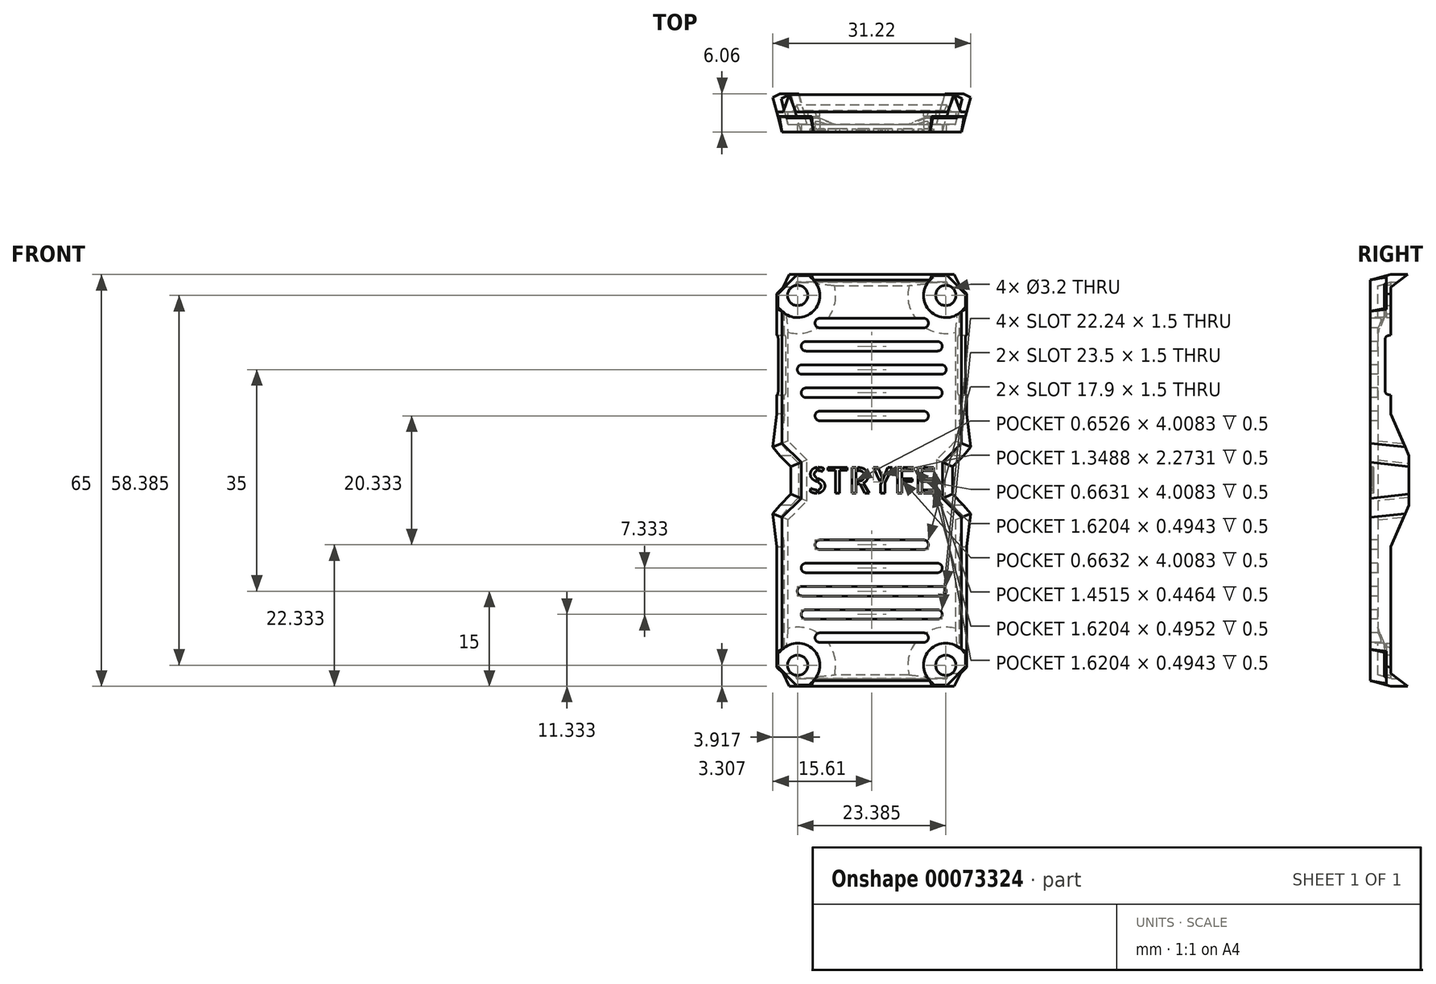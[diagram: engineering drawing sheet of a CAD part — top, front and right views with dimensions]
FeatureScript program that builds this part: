
annotation { "Feature Type Name" : "Feature", "Feature Type Description" : "" }
export const myFeature = defineFeature(function(context is Context, id is Id, definition is map)
    precondition{}
    {
        {
            var Q0;
            Q0=qCreatedBy(makeId("Front.planeOp"),FACE);
            var sketch = newSketch(context, id + "F0", { "sketchPlane" : qUnion([Q0])});
            skLineSegment(sketch, "E0.bottom", {"start": v(15, -32.5) * mm, "end": v(-15, -32.5) * mm});
            skLineSegment(sketch, "E0.top", {"start": v(15, 32.5) * mm, "end": v(-15, 32.5) * mm});
            skLineSegment(sketch, "E0.left", {"start": v(15, -32.5) * mm, "end": v(15, 32.5) * mm});
            skLineSegment(sketch, "E0.right", {"start": v(-15, -32.5) * mm, "end": v(-15, 32.5) * mm});
            skPoint(sketch, "E0.middle", {"position": v(0, 0) * mm});
            skSolve(sketch);
        }
        {
            var Q0;
            Q0=qCreatedBy(makeId("Front.planeOp"),FACE);
            var sketch = newSketch(context, id + "F1", { "sketchPlane" : qUnion([Q0])});
            skLineSegment(sketch, "E1", {"start": v(0, 32.5) * mm, "end": v(-12, 32.5) * mm});
            skLineSegment(sketch, "E2", {"start": v(-12, 32.5) * mm, "end": v(-15, 29.5) * mm});
            skLineSegment(sketch, "E3", {"start": v(-15, 29.5) * mm, "end": v(-15, 5.5) * mm});
            skLineSegment(sketch, "E4", {"start": v(-15, 5.5) * mm, "end": v(-12, 2.5) * mm});
            skLineSegment(sketch, "E5", {"start": v(-12, 2.5) * mm, "end": v(-12, 0) * mm});
            skLineSegment(sketch, "E6", {"start": v(-12, 2.5) * mm, "end": v(-15, 2.5) * mm, "construction": true});
            skLineSegment(sketch, "E7", {"start": v(-15, 2.5) * mm, "end": v(-15, 5.5) * mm, "construction": true});
            skLineSegment(sketch, "E8", {"start": v(-15, 29.5) * mm, "end": v(-15, 32.5) * mm, "construction": true});
            skLineSegment(sketch, "E9", {"start": v(-15, 32.5) * mm, "end": v(-12, 32.5) * mm, "construction": true});
            skLineSegment(sketch, "E10.MirrorCS", {"start": v(0, 32.5) * mm, "end": v(12, 32.5) * mm});
            skLineSegment(sketch, "E11.MirrorCS", {"start": v(12, 2.5) * mm, "end": v(12, 0) * mm});
            skLineSegment(sketch, "E12.MirrorCS", {"start": v(15, 5.5) * mm, "end": v(12, 2.5) * mm});
            skLineSegment(sketch, "E13.MirrorCS", {"start": v(12, 32.5) * mm, "end": v(15, 29.5) * mm});
            skLineSegment(sketch, "E14.MirrorCS", {"start": v(15, 29.5) * mm, "end": v(15, 5.5) * mm});
            skLineSegment(sketch, "E15.MirrorCS", {"start": v(12, -2.5) * mm, "end": v(12, 0) * mm});
            skLineSegment(sketch, "E16.MirrorCS", {"start": v(15, -5.5) * mm, "end": v(12, -2.5) * mm});
            skLineSegment(sketch, "E17.MirrorCS", {"start": v(15, -29.5) * mm, "end": v(15, -5.5) * mm});
            skLineSegment(sketch, "E18.MirrorCS", {"start": v(12, -32.5) * mm, "end": v(15, -29.5) * mm});
            skLineSegment(sketch, "E19.MirrorCS", {"start": v(0, -32.5) * mm, "end": v(12, -32.5) * mm});
            skLineSegment(sketch, "E20.MirrorCS", {"start": v(0, -32.5) * mm, "end": v(-12, -32.5) * mm});
            skLineSegment(sketch, "E21.MirrorCS", {"start": v(-12, -32.5) * mm, "end": v(-15, -29.5) * mm});
            skLineSegment(sketch, "E22.MirrorCS", {"start": v(-15, -29.5) * mm, "end": v(-15, -5.5) * mm});
            skLineSegment(sketch, "E23.MirrorCS", {"start": v(-12, -2.5) * mm, "end": v(-12, 0) * mm});
            skLineSegment(sketch, "E24.MirrorCS", {"start": v(-15, -5.5) * mm, "end": v(-12, -2.5) * mm});
            skLineSegment(sketch, "E25", {"start": v(-12, 32.5) * mm, "end": v(12, 32.5) * mm, "construction": true});
            skSolve(sketch);
        }
        {
            assignVariable(context, id + "F2", {"name" : "Draft", "anyValue" : 15});
        }
        {
            var Q0;
            Q0 = qSketchRegion(id + "F1", true);
            extrude(context, id + "F3", {"entities" : qUnion([Q0]), "depth" : 3.2 * mm, "hasDraft" : true, "draftAngle" : (getVariable(context, 'Draft')) * degree, "draftPullDirection" : true});
        }
        {
            var Q0;
            Q0=qCreatedBy(makeId("Front.planeOp"),FACE);
            var sketch = newSketch(context, id + "F4", { "sketchPlane" : qUnion([Q0])});
            skLineSegment(sketch, "E26.0.1", {"start": v(-15, -10.5) * mm, "end": v(-15, -5.5) * mm});
            skLineSegment(sketch, "E26.0.2", {"start": v(-15, -5.5) * mm, "end": v(-12, -2.5) * mm});
            skLineSegment(sketch, "E26.0.3", {"start": v(-12, 2.5) * mm, "end": v(-12, -2.5) * mm});
            skLineSegment(sketch, "E26.0.4", {"start": v(-15, 5.5) * mm, "end": v(-12, 2.5) * mm});
            skLineSegment(sketch, "E26.0.5", {"start": v(-15, 10.5) * mm, "end": v(-15, 5.5) * mm});
            skLineSegment(sketch, "E26.0.9", {"start": v(15, 10.5) * mm, "end": v(15, 5.5) * mm});
            skLineSegment(sketch, "E26.0.10", {"start": v(15, 5.5) * mm, "end": v(12, 2.5) * mm});
            skLineSegment(sketch, "E26.0.11", {"start": v(12, -2.5) * mm, "end": v(12, 2.5) * mm});
            skLineSegment(sketch, "E26.0.12", {"start": v(15, -5.5) * mm, "end": v(12, -2.5) * mm});
            skLineSegment(sketch, "E26.0.13", {"start": v(15, -10.5) * mm, "end": v(15, -5.5) * mm});
            skLineSegment(sketch, "E27", {"start": v(15, 10.5) * mm, "end": v(-15, 10.5) * mm});
            skLineSegment(sketch, "E28", {"start": v(-15, -10.5) * mm, "end": v(15, -10.5) * mm});
            skLineSegment(sketch, "E29", {"start": v(0, 0) * mm, "end": v(0, 10.5) * mm, "construction": true});
            skLineSegment(sketch, "E30", {"start": v(0, 0) * mm, "end": v(0, -10.5) * mm, "construction": true});
            skSolve(sketch);
        }
        {
            var Q0;
            Q0 = qSketchRegion(id + "F4", true);
            extrude(context, id + "F5", {"entities" : qUnion([Q0]), "operationType" : NewBodyOperationType.ADD, "oppositeDirection" : true, "depth" : 2.86 * mm, "hasDraft" : true, "draftAngle" : (getVariable(context, 'Draft')) * degree});
        }
        {
            var Q0;
            Q0=qCreatedBy(makeId("Right.planeOp"),FACE);
            var sketch = newSketch(context, id + "F6", { "sketchPlane" : qUnion([Q0])});
            skLineSegment(sketch, "E31", {"start": v(0, 10.5) * mm, "end": v(2.86, 3.9) * mm});
            skLineSegment(sketch, "E32", {"start": v(2.86, 3.9) * mm, "end": v(2.86, 0) * mm});
            skLineSegment(sketch, "E33", {"start": v(2.86, 0) * mm, "end": v(0, 0) * mm, "construction": true});
            skLineSegment(sketch, "E34.MirrorCS", {"start": v(0, -10.5) * mm, "end": v(2.86, -3.9) * mm});
            skLineSegment(sketch, "E35.MirrorCS", {"start": v(2.86, -3.9) * mm, "end": v(2.86, 0) * mm});
            skLineSegment(sketch, "E36.0", {"start": v(2.86, 11.27) * mm, "end": v(0, 10.5) * mm});
            skLineSegment(sketch, "E36.1", {"start": v(2.86, -11.27) * mm, "end": v(0, -10.5) * mm});
            skLineSegment(sketch, "E37", {"start": v(2.86, -11.27) * mm, "end": v(2.86, -3.9) * mm});
            skLineSegment(sketch, "E38", {"start": v(2.86, 3.9) * mm, "end": v(2.86, 11.27) * mm});
            skSolve(sketch);
        }
        {
            var Q0;
            Q0 = qSketchRegion(id + "F6", true);
            extrude(context, id + "F7", {"entities" : qUnion([Q0]), "operationType" : NewBodyOperationType.REMOVE, "endBound" : BoundingType.THROUGH_ALL, "depth" : 25 * mm, "hasSecondDirection" : true, "secondDirectionBound" : SecondDirectionBoundingType.THROUGH_ALL, "secondDirectionOppositeDirection" : true, "secondDirectionDepth" : 25 * mm});
        }
        {
            var Q0;
            Q0=qCreatedBy(makeId("Right.planeOp"),FACE);
            var sketch = newSketch(context, id + "F8", { "sketchPlane" : qUnion([Q0])});
            skLineSegment(sketch, "E39", {"start": v(0, 32.5) * mm, "end": v(0, 30.5) * mm});
            skLineSegment(sketch, "E40", {"start": v(0, 30.5) * mm, "end": v(2.7, 32.5) * mm});
            skLineSegment(sketch, "E41", {"start": v(2.7, 32.5) * mm, "end": v(0, 32.5) * mm});
            skLineSegment(sketch, "E42.MirrorCS", {"start": v(0, -32.5) * mm, "end": v(0, -30.5) * mm, "construction": true});
            skLineSegment(sketch, "E43.MirrorCS", {"start": v(0, -30.5) * mm, "end": v(2.7, -32.5) * mm, "construction": true});
            skLineSegment(sketch, "E44.MirrorCS", {"start": v(2.7, -32.5) * mm, "end": v(0, -32.5) * mm, "construction": true});
            skSolve(sketch);
        }
        {
            var Q0;
            Q0 = qSketchRegion(id + "F8", true);
            var Q1;
            Q1=makeQuery(id+"F3.opExtrude","SWEPT_FACE",FACE,{"disambiguationData":[OSD([sQuery(id+"F1.wireOp",EDGE,"E13.MirrorCS")])]});
            var Q2;
            Q2=makeQuery(id+"F3.opExtrude","SWEPT_BODY",BODY,{"disambiguationData":[OSD([sQuery(id+"F1.wireOp",EDGE,"E1"),sQuery(id+"F1.wireOp",EDGE,"E2"),sQuery(id+"F1.wireOp",EDGE,"E3"),sQuery(id+"F1.wireOp",EDGE,"E4"),sQuery(id+"F1.wireOp",EDGE,"E5"),sQuery(id+"F1.wireOp",EDGE,"E10.MirrorCS"),sQuery(id+"F1.wireOp",EDGE,"E11.MirrorCS"),sQuery(id+"F1.wireOp",EDGE,"E12.MirrorCS"),sQuery(id+"F1.wireOp",EDGE,"E13.MirrorCS"),sQuery(id+"F1.wireOp",EDGE,"E14.MirrorCS"),sQuery(id+"F1.wireOp",EDGE,"E15.MirrorCS"),sQuery(id+"F1.wireOp",EDGE,"E16.MirrorCS"),sQuery(id+"F1.wireOp",EDGE,"E17.MirrorCS"),sQuery(id+"F1.wireOp",EDGE,"E18.MirrorCS"),sQuery(id+"F1.wireOp",EDGE,"E19.MirrorCS"),sQuery(id+"F1.wireOp",EDGE,"E20.MirrorCS"),sQuery(id+"F1.wireOp",EDGE,"E21.MirrorCS"),sQuery(id+"F1.wireOp",EDGE,"E22.MirrorCS"),sQuery(id+"F1.wireOp",EDGE,"E23.MirrorCS"),sQuery(id+"F1.wireOp",EDGE,"E24.MirrorCS")])]});
            var Q3;
            Q3=makeQuery(id+"F3.opExtrude","SWEPT_FACE",FACE,{"disambiguationData":[OSD([sQuery(id+"F1.wireOp",EDGE,"E2")])]});
            extrude(context, id + "F9", {"entities" : qUnion([Q0]), "operationType" : NewBodyOperationType.ADD, "endBound" : BoundingType.UP_TO_SURFACE, "endBoundEntityFace" : qUnion([Q1]), "endBoundEntityBody" : qUnion([Q2]), "depth" : 25 * mm, "hasSecondDirection" : true, "secondDirectionBound" : SecondDirectionBoundingType.UP_TO_SURFACE, "secondDirectionOppositeDirection" : true, "secondDirectionBoundEntityFace" : qUnion([Q3]), "secondDirectionDepth" : 25 * mm});
        }
        {
            var Q0;
            Q0=qCreatedBy(makeId("Right.planeOp"),FACE);
            var sketch = newSketch(context, id + "F10", { "sketchPlane" : qUnion([Q0])});
            skLineSegment(sketch, "E45.0", {"start": v(0, -30.5) * mm, "end": v(2.7, -32.5) * mm});
            skLineSegment(sketch, "E45.1", {"start": v(0, -32.5) * mm, "end": v(0, -30.5) * mm});
            skLineSegment(sketch, "E45.2", {"start": v(2.7, -32.5) * mm, "end": v(0, -32.5) * mm});
            skSolve(sketch);
        }
        {
            var Q0;
            Q0 = qSketchRegion(id + "F10", true);
            var Q1;
            Q1=makeQuery(id+"F3.opExtrude","SWEPT_FACE",FACE,{"disambiguationData":[OSD([sQuery(id+"F1.wireOp",EDGE,"E21.MirrorCS")])]});
            var Q2;
            Q2=makeQuery(id+"F3.opExtrude","SWEPT_FACE",FACE,{"disambiguationData":[OSD([sQuery(id+"F1.wireOp",EDGE,"E18.MirrorCS")])]});
            extrude(context, id + "F11", {"entities" : qUnion([Q0]), "operationType" : NewBodyOperationType.ADD, "endBound" : BoundingType.UP_TO_SURFACE, "oppositeDirection" : true, "endBoundEntityFace" : qUnion([Q1]), "depth" : 25 * mm, "hasSecondDirection" : true, "secondDirectionBound" : SecondDirectionBoundingType.UP_TO_SURFACE, "secondDirectionOppositeDirection" : false, "secondDirectionBoundEntityFace" : qUnion([Q2]), "secondDirectionDepth" : 25 * mm});
        }
        {
            var Q0;
            {var subQ0=sQuery(id+"F1.wireOp",EDGE,"E3");var subQ1=sQuery(id+"F1.wireOp",EDGE,"E13.MirrorCS");var subQ2=sQuery(id+"F1.wireOp",EDGE,"E2");var subQ3=sQuery(id+"F1.wireOp",EDGE,"E10.MirrorCS");var subQ4=sQuery(id+"F1.wireOp",EDGE,"E1");var subQ5=sQuery(id+"F1.wireOp",EDGE,"E14.MirrorCS");Q0=makeQuery(id+"F5.boolean.opBoolean","SPLIT",FACE,{"disambiguationData":[TD([makeQuery(id+"F3.opExtrude","SWEPT_FACE",FACE,{"disambiguationData":[OSD([subQ2])]})])],"derivedFrom":makeQuery(id+"F3.opExtrude","CAP_FACE",FACE,{"disambiguationData":[OSD([subQ4,subQ2,subQ0,sQuery(id+"F1.wireOp",EDGE,"E4"),sQuery(id+"F1.wireOp",EDGE,"E5"),subQ3,sQuery(id+"F1.wireOp",EDGE,"E11.MirrorCS"),sQuery(id+"F1.wireOp",EDGE,"E12.MirrorCS"),subQ1,subQ5,sQuery(id+"F1.wireOp",EDGE,"E15.MirrorCS"),sQuery(id+"F1.wireOp",EDGE,"E16.MirrorCS"),sQuery(id+"F1.wireOp",EDGE,"E17.MirrorCS"),sQuery(id+"F1.wireOp",EDGE,"E18.MirrorCS"),sQuery(id+"F1.wireOp",EDGE,"E19.MirrorCS"),sQuery(id+"F1.wireOp",EDGE,"E20.MirrorCS"),sQuery(id+"F1.wireOp",EDGE,"E21.MirrorCS"),sQuery(id+"F1.wireOp",EDGE,"E22.MirrorCS"),sQuery(id+"F1.wireOp",EDGE,"E23.MirrorCS"),sQuery(id+"F1.wireOp",EDGE,"E24.MirrorCS")])],"isStart":true})});}
            var Q1;
            Q1=makeQuery(id+"F7.boolean.opBoolean","COPY",FACE,{"derivedFrom":makeQuery(id+"F7.opExtrude","SWEPT_FACE",FACE,{"disambiguationData":[OSD([sQuery(id+"F6.wireOp",EDGE,"E31")])]})});
            var Q2;
            Q2=makeQuery(id+"F5.opExtrude","CAP_FACE",FACE,{"disambiguationData":[OSD([sQuery(id+"F4.wireOp",EDGE,"E26.0.1"),sQuery(id+"F4.wireOp",EDGE,"E26.0.2"),sQuery(id+"F4.wireOp",EDGE,"E26.0.3"),sQuery(id+"F4.wireOp",EDGE,"E26.0.4"),sQuery(id+"F4.wireOp",EDGE,"E26.0.5"),sQuery(id+"F4.wireOp",EDGE,"E26.0.9"),sQuery(id+"F4.wireOp",EDGE,"E26.0.10"),sQuery(id+"F4.wireOp",EDGE,"E26.0.11"),sQuery(id+"F4.wireOp",EDGE,"E26.0.12"),sQuery(id+"F4.wireOp",EDGE,"E26.0.13"),sQuery(id+"F4.wireOp",EDGE,"E27"),sQuery(id+"F4.wireOp",EDGE,"E28")])],"isStart":false});
            var Q3;
            Q3=makeQuery(id+"F7.boolean.opBoolean","COPY",FACE,{"derivedFrom":makeQuery(id+"F7.opExtrude","SWEPT_FACE",FACE,{"disambiguationData":[OSD([sQuery(id+"F6.wireOp",EDGE,"E34.MirrorCS")])]})});
            var Q4;
            {var subQ0=sQuery(id+"F1.wireOp",EDGE,"E21.MirrorCS");var subQ1=sQuery(id+"F1.wireOp",EDGE,"E20.MirrorCS");var subQ2=sQuery(id+"F1.wireOp",EDGE,"E19.MirrorCS");var subQ3=sQuery(id+"F1.wireOp",EDGE,"E18.MirrorCS");var subQ4=sQuery(id+"F1.wireOp",EDGE,"E17.MirrorCS");var subQ5=sQuery(id+"F1.wireOp",EDGE,"E22.MirrorCS");Q4=makeQuery(id+"F5.boolean.opBoolean","SPLIT",FACE,{"disambiguationData":[TD([makeQuery(id+"F3.opExtrude","SWEPT_FACE",FACE,{"disambiguationData":[OSD([subQ4])]})])],"derivedFrom":makeQuery(id+"F3.opExtrude","CAP_FACE",FACE,{"disambiguationData":[OSD([sQuery(id+"F1.wireOp",EDGE,"E1"),sQuery(id+"F1.wireOp",EDGE,"E2"),sQuery(id+"F1.wireOp",EDGE,"E3"),sQuery(id+"F1.wireOp",EDGE,"E4"),sQuery(id+"F1.wireOp",EDGE,"E5"),sQuery(id+"F1.wireOp",EDGE,"E10.MirrorCS"),sQuery(id+"F1.wireOp",EDGE,"E11.MirrorCS"),sQuery(id+"F1.wireOp",EDGE,"E12.MirrorCS"),sQuery(id+"F1.wireOp",EDGE,"E13.MirrorCS"),sQuery(id+"F1.wireOp",EDGE,"E14.MirrorCS"),sQuery(id+"F1.wireOp",EDGE,"E15.MirrorCS"),sQuery(id+"F1.wireOp",EDGE,"E16.MirrorCS"),subQ4,subQ3,subQ2,subQ1,subQ0,subQ5,sQuery(id+"F1.wireOp",EDGE,"E23.MirrorCS"),sQuery(id+"F1.wireOp",EDGE,"E24.MirrorCS")])],"isStart":true})});}
            var Q5;
            Q5=makeQuery(id+"F9.opExtrude","SWEPT_FACE",FACE,{"disambiguationData":[OSD([sQuery(id+"F8.wireOp",EDGE,"E40")])]});
            var Q6;
            Q6=makeQuery(id+"F11.opExtrude","SWEPT_FACE",FACE,{"disambiguationData":[OSD([sQuery(id+"F10.wireOp",EDGE,"E45.0")])]});
            shell(context, id + "F12", {"entities" : qUnion([Q0, Q1, Q2, Q3, Q4, Q5, Q6]), "thickness" : 1.2 * mm});
        }
        {
            var Q0;
            Q0=qCreatedBy(makeId("Right.planeOp"),FACE);
            var sketch = newSketch(context, id + "F13", { "sketchPlane" : qUnion([Q0])});
            skLineSegment(sketch, "E46.bottom", {"start": v(0, 22.9) * mm, "end": v(-0.2, 22.9) * mm});
            skLineSegment(sketch, "E46.top", {"start": v(0, 13.5) * mm, "end": v(-0.2, 13.5) * mm});
            skLineSegment(sketch, "E46.left", {"start": v(0, 22.9) * mm, "end": v(0, 13.5) * mm});
            skLineSegment(sketch, "E46.right", {"start": v(-0.9, 22.2) * mm, "end": v(-0.9, 14.2) * mm});
            skPoint(sketch, "E47.visualSharp", {"position": v(-0.9, 22.9) * mm});
            skArc(sketch, "E47.filletArc", {"start": v(-0.2, 22.9) * mm, "mid": v(-0.7, 22.7) * mm, "end": v(-0.9, 22.2) * mm});
            skPoint(sketch, "E48.visualSharp", {"position": v(-0.9, 13.5) * mm});
            skArc(sketch, "E48.filletArc", {"start": v(-0.9, 14.2) * mm, "mid": v(-0.7, 13.7) * mm, "end": v(-0.2, 13.5) * mm});
            skSolve(sketch);
        }
        {
            var Q0;
            Q0 = qSketchRegion(id + "F13", true);
            extrude(context, id + "F14", {"entities" : qUnion([Q0]), "operationType" : NewBodyOperationType.REMOVE, "endBound" : BoundingType.THROUGH_ALL, "oppositeDirection" : true, "depth" : 25 * mm, "hasSecondDirection" : true, "secondDirectionBound" : SecondDirectionBoundingType.THROUGH_ALL, "secondDirectionOppositeDirection" : false, "secondDirectionDepth" : 25 * mm});
        }
        {
            var Q0;
            Q0=makeQuery(id+"F3.opExtrude","CAP_FACE",FACE,{"disambiguationData":[OSD([sQuery(id+"F1.wireOp",EDGE,"E1"),sQuery(id+"F1.wireOp",EDGE,"E2"),sQuery(id+"F1.wireOp",EDGE,"E3"),sQuery(id+"F1.wireOp",EDGE,"E4"),sQuery(id+"F1.wireOp",EDGE,"E5"),sQuery(id+"F1.wireOp",EDGE,"E10.MirrorCS"),sQuery(id+"F1.wireOp",EDGE,"E11.MirrorCS"),sQuery(id+"F1.wireOp",EDGE,"E12.MirrorCS"),sQuery(id+"F1.wireOp",EDGE,"E13.MirrorCS"),sQuery(id+"F1.wireOp",EDGE,"E14.MirrorCS"),sQuery(id+"F1.wireOp",EDGE,"E15.MirrorCS"),sQuery(id+"F1.wireOp",EDGE,"E16.MirrorCS"),sQuery(id+"F1.wireOp",EDGE,"E17.MirrorCS"),sQuery(id+"F1.wireOp",EDGE,"E18.MirrorCS"),sQuery(id+"F1.wireOp",EDGE,"E19.MirrorCS"),sQuery(id+"F1.wireOp",EDGE,"E20.MirrorCS"),sQuery(id+"F1.wireOp",EDGE,"E21.MirrorCS"),sQuery(id+"F1.wireOp",EDGE,"E22.MirrorCS"),sQuery(id+"F1.wireOp",EDGE,"E23.MirrorCS"),sQuery(id+"F1.wireOp",EDGE,"E24.MirrorCS")])],"isStart":false});
            var sketch = newSketch(context, id + "F15", { "sketchPlane" : qUnion([Q0])});
            skCircle(sketch, "E49", {"center": v(-11.7, 29.2) * mm, "radius": 3.5 * mm});
            skCircle(sketch, "E50", {"center": v(-11.7, 29.2) * mm, "radius": 1.6 * mm});
            skCircle(sketch, "E51", {"center": v(-11.7, 29.2) * mm, "radius": 4 * mm});
            skCircle(sketch, "E52.MirrorC", {"center": v(11.7, 29.2) * mm, "radius": 1.6 * mm});
            skCircle(sketch, "E53.MirrorC", {"center": v(11.7, 29.2) * mm, "radius": 3.5 * mm});
            skCircle(sketch, "E54.MirrorC", {"center": v(11.7, 29.2) * mm, "radius": 4 * mm});
            skCircle(sketch, "E55.MirrorC", {"center": v(11.7, -29.2) * mm, "radius": 1.6 * mm});
            skCircle(sketch, "E56.MirrorC", {"center": v(11.7, -29.2) * mm, "radius": 3.5 * mm});
            skCircle(sketch, "E57.MirrorC", {"center": v(11.7, -29.2) * mm, "radius": 4 * mm});
            skCircle(sketch, "E58.MirrorC", {"center": v(-11.7, -29.2) * mm, "radius": 1.6 * mm});
            skCircle(sketch, "E59.MirrorC", {"center": v(-11.7, -29.2) * mm, "radius": 3.5 * mm});
            skCircle(sketch, "E60.MirrorC", {"center": v(-11.7, -29.2) * mm, "radius": 4 * mm});
            skSolve(sketch);
        }
        {
            var Q0;
            Q0=makeQuery(id+"F15.imprint","IMPRINT",FACE,{"disambiguationData":[TD([[makeQuery(id+"F15.imprint","IMPRINT",EDGE,{"derivedFrom":sQuery(id+"F15.wireOp",EDGE,"E51")}),-1.0]])]});
            var sketch = newSketch(context, id + "F16", { "sketchPlane" : qUnion([Q0])});
            skCircle(sketch, "E61.0", {"center": v(-11.7, 29.2) * mm, "radius": 1.6 * mm});
            skCircle(sketch, "E61.1", {"center": v(11.7, 29.2) * mm, "radius": 1.6 * mm});
            skCircle(sketch, "E61.2", {"center": v(11.7, -29.2) * mm, "radius": 1.6 * mm});
            skCircle(sketch, "E61.3", {"center": v(-11.7, -29.2) * mm, "radius": 1.6 * mm});
            skSolve(sketch);
        }
        {
            var Q0;
            Q0=qCreatedBy(makeId("Front.planeOp"),FACE);
            var sketch = newSketch(context, id + "F17", { "sketchPlane" : qUnion([Q0])});
            skCircle(sketch, "E62.0", {"center": v(11.7, 29.2) * mm, "radius": 3.5 * mm});
            skCircle(sketch, "E62.1", {"center": v(-11.7, 29.2) * mm, "radius": 3.5 * mm});
            skCircle(sketch, "E62.2", {"center": v(-11.7, -29.2) * mm, "radius": 3.5 * mm});
            skCircle(sketch, "E62.3", {"center": v(11.7, -29.2) * mm, "radius": 3.5 * mm});
            skSolve(sketch);
        }
        {
            var Q0;
            Q0=makeQuery(id+"F15.imprint","IMPRINT",FACE,{"disambiguationData":[TD([[makeQuery(id+"F15.imprint","IMPRINT",EDGE,{"derivedFrom":sQuery(id+"F15.wireOp",EDGE,"E51")}),-1.0]])]});
            var sketch = newSketch(context, id + "F18", { "sketchPlane" : qUnion([Q0])});
            skCircle(sketch, "E63.0", {"center": v(-11.7, 29.2) * mm, "radius": 3.5 * mm});
            skCircle(sketch, "E63.1", {"center": v(11.7, 29.2) * mm, "radius": 3.5 * mm});
            skCircle(sketch, "E63.2", {"center": v(11.7, -29.2) * mm, "radius": 3.5 * mm});
            skCircle(sketch, "E63.3", {"center": v(-11.7, -29.2) * mm, "radius": 3.5 * mm});
            skSolve(sketch);
        }
        {
            var Q0;
            Q0 = qSketchRegion(id + "F17", true);
            var Q1;
            Q1=makeQuery(id+"F3.opExtrude","SWEPT_BODY",BODY,{"disambiguationData":[OSD([sQuery(id+"F1.wireOp",EDGE,"E1"),sQuery(id+"F1.wireOp",EDGE,"E2"),sQuery(id+"F1.wireOp",EDGE,"E3"),sQuery(id+"F1.wireOp",EDGE,"E4"),sQuery(id+"F1.wireOp",EDGE,"E5"),sQuery(id+"F1.wireOp",EDGE,"E10.MirrorCS"),sQuery(id+"F1.wireOp",EDGE,"E11.MirrorCS"),sQuery(id+"F1.wireOp",EDGE,"E12.MirrorCS"),sQuery(id+"F1.wireOp",EDGE,"E13.MirrorCS"),sQuery(id+"F1.wireOp",EDGE,"E14.MirrorCS"),sQuery(id+"F1.wireOp",EDGE,"E15.MirrorCS"),sQuery(id+"F1.wireOp",EDGE,"E16.MirrorCS"),sQuery(id+"F1.wireOp",EDGE,"E17.MirrorCS"),sQuery(id+"F1.wireOp",EDGE,"E18.MirrorCS"),sQuery(id+"F1.wireOp",EDGE,"E19.MirrorCS"),sQuery(id+"F1.wireOp",EDGE,"E20.MirrorCS"),sQuery(id+"F1.wireOp",EDGE,"E21.MirrorCS"),sQuery(id+"F1.wireOp",EDGE,"E22.MirrorCS"),sQuery(id+"F1.wireOp",EDGE,"E23.MirrorCS"),sQuery(id+"F1.wireOp",EDGE,"E24.MirrorCS")])]});
            extrude(context, id + "F19", {"entities" : qUnion([Q0]), "operationType" : NewBodyOperationType.ADD, "endBound" : BoundingType.UP_TO_BODY, "endBoundEntityBody" : qUnion([Q1]), "depth" : 25 * mm});
        }
        {
            var Q0;
            Q0=makeQuery(id+"F19.boolean.opBoolean","INTERSECT",EDGE,{"derivedFrom":[makeQuery(id+"F12.opShell","OFFSET_FACE",FACE,{"disambiguationData":[OSD([sQuery(id+"F1.wireOp",EDGE,"E1"),sQuery(id+"F1.wireOp",EDGE,"E2"),sQuery(id+"F1.wireOp",EDGE,"E3"),sQuery(id+"F1.wireOp",EDGE,"E4"),sQuery(id+"F1.wireOp",EDGE,"E5"),sQuery(id+"F1.wireOp",EDGE,"E10.MirrorCS"),sQuery(id+"F1.wireOp",EDGE,"E11.MirrorCS"),sQuery(id+"F1.wireOp",EDGE,"E12.MirrorCS"),sQuery(id+"F1.wireOp",EDGE,"E13.MirrorCS"),sQuery(id+"F1.wireOp",EDGE,"E14.MirrorCS"),sQuery(id+"F1.wireOp",EDGE,"E15.MirrorCS"),sQuery(id+"F1.wireOp",EDGE,"E16.MirrorCS"),sQuery(id+"F1.wireOp",EDGE,"E17.MirrorCS"),sQuery(id+"F1.wireOp",EDGE,"E18.MirrorCS"),sQuery(id+"F1.wireOp",EDGE,"E19.MirrorCS"),sQuery(id+"F1.wireOp",EDGE,"E20.MirrorCS"),sQuery(id+"F1.wireOp",EDGE,"E21.MirrorCS"),sQuery(id+"F1.wireOp",EDGE,"E22.MirrorCS"),sQuery(id+"F1.wireOp",EDGE,"E23.MirrorCS"),sQuery(id+"F1.wireOp",EDGE,"E24.MirrorCS")])]}),makeQuery(id+"F19.opExtrude","SWEPT_FACE",FACE,{"disambiguationData":[OSD([sQuery(id+"F17.wireOp",EDGE,"E62.0")])]})]});
            var Q1;
            Q1=makeQuery(id+"F19.boolean.opBoolean","INTERSECT",EDGE,{"derivedFrom":[makeQuery(id+"F12.opShell","OFFSET_FACE",FACE,{"disambiguationData":[OSD([sQuery(id+"F1.wireOp",EDGE,"E1"),sQuery(id+"F1.wireOp",EDGE,"E2"),sQuery(id+"F1.wireOp",EDGE,"E3"),sQuery(id+"F1.wireOp",EDGE,"E4"),sQuery(id+"F1.wireOp",EDGE,"E5"),sQuery(id+"F1.wireOp",EDGE,"E10.MirrorCS"),sQuery(id+"F1.wireOp",EDGE,"E11.MirrorCS"),sQuery(id+"F1.wireOp",EDGE,"E12.MirrorCS"),sQuery(id+"F1.wireOp",EDGE,"E13.MirrorCS"),sQuery(id+"F1.wireOp",EDGE,"E14.MirrorCS"),sQuery(id+"F1.wireOp",EDGE,"E15.MirrorCS"),sQuery(id+"F1.wireOp",EDGE,"E16.MirrorCS"),sQuery(id+"F1.wireOp",EDGE,"E17.MirrorCS"),sQuery(id+"F1.wireOp",EDGE,"E18.MirrorCS"),sQuery(id+"F1.wireOp",EDGE,"E19.MirrorCS"),sQuery(id+"F1.wireOp",EDGE,"E20.MirrorCS"),sQuery(id+"F1.wireOp",EDGE,"E21.MirrorCS"),sQuery(id+"F1.wireOp",EDGE,"E22.MirrorCS"),sQuery(id+"F1.wireOp",EDGE,"E23.MirrorCS"),sQuery(id+"F1.wireOp",EDGE,"E24.MirrorCS")])]}),makeQuery(id+"F19.opExtrude","SWEPT_FACE",FACE,{"disambiguationData":[OSD([sQuery(id+"F17.wireOp",EDGE,"E62.1")])]})]});
            var Q2;
            Q2=makeQuery(id+"F19.boolean.opBoolean","INTERSECT",EDGE,{"derivedFrom":[makeQuery(id+"F12.opShell","OFFSET_FACE",FACE,{"disambiguationData":[OSD([sQuery(id+"F1.wireOp",EDGE,"E1"),sQuery(id+"F1.wireOp",EDGE,"E2"),sQuery(id+"F1.wireOp",EDGE,"E3"),sQuery(id+"F1.wireOp",EDGE,"E4"),sQuery(id+"F1.wireOp",EDGE,"E5"),sQuery(id+"F1.wireOp",EDGE,"E10.MirrorCS"),sQuery(id+"F1.wireOp",EDGE,"E11.MirrorCS"),sQuery(id+"F1.wireOp",EDGE,"E12.MirrorCS"),sQuery(id+"F1.wireOp",EDGE,"E13.MirrorCS"),sQuery(id+"F1.wireOp",EDGE,"E14.MirrorCS"),sQuery(id+"F1.wireOp",EDGE,"E15.MirrorCS"),sQuery(id+"F1.wireOp",EDGE,"E16.MirrorCS"),sQuery(id+"F1.wireOp",EDGE,"E17.MirrorCS"),sQuery(id+"F1.wireOp",EDGE,"E18.MirrorCS"),sQuery(id+"F1.wireOp",EDGE,"E19.MirrorCS"),sQuery(id+"F1.wireOp",EDGE,"E20.MirrorCS"),sQuery(id+"F1.wireOp",EDGE,"E21.MirrorCS"),sQuery(id+"F1.wireOp",EDGE,"E22.MirrorCS"),sQuery(id+"F1.wireOp",EDGE,"E23.MirrorCS"),sQuery(id+"F1.wireOp",EDGE,"E24.MirrorCS")])]}),makeQuery(id+"F19.opExtrude","SWEPT_FACE",FACE,{"disambiguationData":[OSD([sQuery(id+"F17.wireOp",EDGE,"E62.3")])]})]});
            var Q3;
            Q3=makeQuery(id+"F19.boolean.opBoolean","INTERSECT",EDGE,{"derivedFrom":[makeQuery(id+"F12.opShell","OFFSET_FACE",FACE,{"disambiguationData":[OSD([sQuery(id+"F1.wireOp",EDGE,"E1"),sQuery(id+"F1.wireOp",EDGE,"E2"),sQuery(id+"F1.wireOp",EDGE,"E3"),sQuery(id+"F1.wireOp",EDGE,"E4"),sQuery(id+"F1.wireOp",EDGE,"E5"),sQuery(id+"F1.wireOp",EDGE,"E10.MirrorCS"),sQuery(id+"F1.wireOp",EDGE,"E11.MirrorCS"),sQuery(id+"F1.wireOp",EDGE,"E12.MirrorCS"),sQuery(id+"F1.wireOp",EDGE,"E13.MirrorCS"),sQuery(id+"F1.wireOp",EDGE,"E14.MirrorCS"),sQuery(id+"F1.wireOp",EDGE,"E15.MirrorCS"),sQuery(id+"F1.wireOp",EDGE,"E16.MirrorCS"),sQuery(id+"F1.wireOp",EDGE,"E17.MirrorCS"),sQuery(id+"F1.wireOp",EDGE,"E18.MirrorCS"),sQuery(id+"F1.wireOp",EDGE,"E19.MirrorCS"),sQuery(id+"F1.wireOp",EDGE,"E20.MirrorCS"),sQuery(id+"F1.wireOp",EDGE,"E21.MirrorCS"),sQuery(id+"F1.wireOp",EDGE,"E22.MirrorCS"),sQuery(id+"F1.wireOp",EDGE,"E23.MirrorCS"),sQuery(id+"F1.wireOp",EDGE,"E24.MirrorCS")])]}),makeQuery(id+"F19.opExtrude","SWEPT_FACE",FACE,{"disambiguationData":[OSD([sQuery(id+"F17.wireOp",EDGE,"E62.2")])]})]});
            chamfer(context, id + "F20", {"entities" : qUnion([Q0, Q1, Q2, Q3]), "chamferType" : ChamferType.TWO_OFFSETS, "width1" : 1 * mm, "oppositeDirection" : false, "width2" : 2.5 * mm, "tangentPropagation" : true});
        }
        {
            var Q0;
            Q0 = qSketchRegion(id + "F16", true);
            extrude(context, id + "F21", {"entities" : qUnion([Q0]), "operationType" : NewBodyOperationType.REMOVE, "endBound" : BoundingType.THROUGH_ALL, "oppositeDirection" : true, "depth" : 25 * mm});
        }
        {
            var Q0;
            Q0 = qSketchRegion(id + "F18", true);
            extrude(context, id + "F22", {"entities" : qUnion([Q0]), "operationType" : NewBodyOperationType.REMOVE, "oppositeDirection" : true, "depth" : 2.5 * mm});
        }
        {
            var Q0;
            Q0=makeQuery(id+"F3.opExtrude","CAP_FACE",FACE,{"disambiguationData":[OSD([sQuery(id+"F1.wireOp",EDGE,"E1"),sQuery(id+"F1.wireOp",EDGE,"E2"),sQuery(id+"F1.wireOp",EDGE,"E3"),sQuery(id+"F1.wireOp",EDGE,"E4"),sQuery(id+"F1.wireOp",EDGE,"E5"),sQuery(id+"F1.wireOp",EDGE,"E10.MirrorCS"),sQuery(id+"F1.wireOp",EDGE,"E11.MirrorCS"),sQuery(id+"F1.wireOp",EDGE,"E12.MirrorCS"),sQuery(id+"F1.wireOp",EDGE,"E13.MirrorCS"),sQuery(id+"F1.wireOp",EDGE,"E14.MirrorCS"),sQuery(id+"F1.wireOp",EDGE,"E15.MirrorCS"),sQuery(id+"F1.wireOp",EDGE,"E16.MirrorCS"),sQuery(id+"F1.wireOp",EDGE,"E17.MirrorCS"),sQuery(id+"F1.wireOp",EDGE,"E18.MirrorCS"),sQuery(id+"F1.wireOp",EDGE,"E19.MirrorCS"),sQuery(id+"F1.wireOp",EDGE,"E20.MirrorCS"),sQuery(id+"F1.wireOp",EDGE,"E21.MirrorCS"),sQuery(id+"F1.wireOp",EDGE,"E22.MirrorCS"),sQuery(id+"F1.wireOp",EDGE,"E23.MirrorCS"),sQuery(id+"F1.wireOp",EDGE,"E24.MirrorCS")])],"isStart":false});
            var sketch = newSketch(context, id + "F23", { "sketchPlane" : qUnion([Q0])});
            skLineSegment(sketch, "E64", {"start": v(-6.34, 34.5) * mm, "end": v(-17, 34.5) * mm});
            skLineSegment(sketch, "E65", {"start": v(-17, 34.5) * mm, "end": v(-17, 23.84) * mm});
            skLineSegment(sketch, "E66", {"start": v(-17, 23.84) * mm, "end": v(-6.34, 34.5) * mm});
            skLineSegment(sketch, "E67.MirrorCS", {"start": v(17, 34.5) * mm, "end": v(17, 23.84) * mm});
            skLineSegment(sketch, "E68.MirrorCS", {"start": v(6.34, 34.5) * mm, "end": v(17, 34.5) * mm});
            skLineSegment(sketch, "E69.MirrorCS", {"start": v(17, 23.84) * mm, "end": v(6.34, 34.5) * mm});
            skLineSegment(sketch, "E70.MirrorCS", {"start": v(17, -34.5) * mm, "end": v(17, -23.84) * mm});
            skLineSegment(sketch, "E71.MirrorCS", {"start": v(17, -23.84) * mm, "end": v(6.34, -34.5) * mm});
            skLineSegment(sketch, "E72.MirrorCS", {"start": v(6.34, -34.5) * mm, "end": v(17, -34.5) * mm});
            skLineSegment(sketch, "E73.MirrorCS", {"start": v(-17, -23.84) * mm, "end": v(-6.34, -34.5) * mm});
            skLineSegment(sketch, "E74.MirrorCS", {"start": v(-6.34, -34.5) * mm, "end": v(-17, -34.5) * mm});
            skLineSegment(sketch, "E75.MirrorCS", {"start": v(-17, -34.5) * mm, "end": v(-17, -23.84) * mm});
            skSolve(sketch);
        }
        {
            var Q0;
            Q0 = qSketchRegion(id + "F23", true);
            var Q1;
            Q1=makeQuery(id+"F22.boolean.opBoolean","COPY",FACE,{"derivedFrom":makeQuery(id+"F22.opExtrude","CAP_FACE",FACE,{"disambiguationData":[OSD([sQuery(id+"F18.wireOp",EDGE,"E63.0")])],"isStart":false})});
            extrude(context, id + "F24", {"entities" : qUnion([Q0]), "operationType" : NewBodyOperationType.REMOVE, "endBound" : BoundingType.UP_TO_SURFACE, "oppositeDirection" : true, "endBoundEntityFace" : qUnion([Q1]), "depth" : 25 * mm, "hasDraft" : true, "draftAngle" : (getVariable(context, 'Draft')) * degree, "draftPullDirection" : true});
        }
        {
            var Q0;
            Q0=makeQuery(id+"F3.opExtrude","CAP_FACE",FACE,{"disambiguationData":[OSD([sQuery(id+"F1.wireOp",EDGE,"E1"),sQuery(id+"F1.wireOp",EDGE,"E2"),sQuery(id+"F1.wireOp",EDGE,"E3"),sQuery(id+"F1.wireOp",EDGE,"E4"),sQuery(id+"F1.wireOp",EDGE,"E5"),sQuery(id+"F1.wireOp",EDGE,"E10.MirrorCS"),sQuery(id+"F1.wireOp",EDGE,"E11.MirrorCS"),sQuery(id+"F1.wireOp",EDGE,"E12.MirrorCS"),sQuery(id+"F1.wireOp",EDGE,"E13.MirrorCS"),sQuery(id+"F1.wireOp",EDGE,"E14.MirrorCS"),sQuery(id+"F1.wireOp",EDGE,"E15.MirrorCS"),sQuery(id+"F1.wireOp",EDGE,"E16.MirrorCS"),sQuery(id+"F1.wireOp",EDGE,"E17.MirrorCS"),sQuery(id+"F1.wireOp",EDGE,"E18.MirrorCS"),sQuery(id+"F1.wireOp",EDGE,"E19.MirrorCS"),sQuery(id+"F1.wireOp",EDGE,"E20.MirrorCS"),sQuery(id+"F1.wireOp",EDGE,"E21.MirrorCS"),sQuery(id+"F1.wireOp",EDGE,"E22.MirrorCS"),sQuery(id+"F1.wireOp",EDGE,"E23.MirrorCS"),sQuery(id+"F1.wireOp",EDGE,"E24.MirrorCS")])],"isStart":false});
            var sketch = newSketch(context, id + "F25", { "sketchPlane" : qUnion([Q0])});
            skCircle(sketch, "E76", {"center": v(0, 17.5) * mm, "radius": 11 * mm, "construction": true});
            skLineSegment(sketch, "E77", {"start": v(-11, 17.5) * mm, "end": v(11, 17.5) * mm});
            skLineSegment(sketch, "E78", {"start": v(10.37, 21.17) * mm, "end": v(-10.37, 21.17) * mm});
            skLineSegment(sketch, "E79", {"start": v(-8.2, 24.83) * mm, "end": v(8.2, 24.83) * mm});
            skLineSegment(sketch, "E80", {"start": v(10.37, 13.83) * mm, "end": v(-10.37, 13.83) * mm});
            skLineSegment(sketch, "E81", {"start": v(-8.2, 10.17) * mm, "end": v(8.2, 10.17) * mm});
            skLineSegment(sketch, "E82", {"start": v(0, 28.5) * mm, "end": v(0, 24.83) * mm});
            skLineSegment(sketch, "E83", {"start": v(0, 24.83) * mm, "end": v(0, 21.17) * mm});
            skLineSegment(sketch, "E84", {"start": v(0, 21.17) * mm, "end": v(0, 17.5) * mm});
            skLineSegment(sketch, "E85", {"start": v(0, 13.83) * mm, "end": v(0, 10.17) * mm});
            skLineSegment(sketch, "E86", {"start": v(0, 10.17) * mm, "end": v(0, 6.5) * mm});
            skLineSegment(sketch, "E87", {"start": v(0, 17.5) * mm, "end": v(0, 13.83) * mm});
            skSolve(sketch);
        }
        {
            var Q0;
            Q0=makeQuery(id+"F25.imprint","IMPRINT",FACE,{"disambiguationData":[TD([[makeQuery(id+"F25.imprint","IMPRINT",EDGE,{"derivedFrom":makeQuery(id+"F3.opExtrude","CAP_EDGE",EDGE,{"disambiguationData":[OSD([sQuery(id+"F1.wireOp",EDGE,"E4")])],"isStart":false})}),1.0]])]});
            var sketch = newSketch(context, id + "F26", { "sketchPlane" : qUnion([Q0])});
            skLineSegment(sketch, "E88.0", {"start": v(-8.2, 24.83) * mm, "end": v(8.2, 24.83) * mm, "construction": true});
            skLineSegment(sketch, "E88.1", {"start": v(10.37, 21.17) * mm, "end": v(-10.37, 21.17) * mm, "construction": true});
            skLineSegment(sketch, "E88.2", {"start": v(-11, 17.5) * mm, "end": v(11, 17.5) * mm, "construction": true});
            skLineSegment(sketch, "E88.3", {"start": v(10.37, 13.83) * mm, "end": v(-10.37, 13.83) * mm, "construction": true});
            skLineSegment(sketch, "E88.4", {"start": v(-8.2, 10.17) * mm, "end": v(8.2, 10.17) * mm, "construction": true});
            skArc(sketch, "E89.0.startCap", {"start": v(-8.2, 24.08) * mm, "mid": v(-8.95, 24.83) * mm, "end": v(-8.2, 25.58) * mm});
            skArc(sketch, "E89.0.endCap", {"start": v(8.2, 25.58) * mm, "mid": v(8.95, 24.83) * mm, "end": v(8.2, 24.08) * mm});
            skLineSegment(sketch, "E89.0.left", {"start": v(-8.2, 25.58) * mm, "end": v(8.2, 25.58) * mm});
            skLineSegment(sketch, "E89.0.right", {"start": v(-8.2, 24.08) * mm, "end": v(8.2, 24.08) * mm});
            skArc(sketch, "E89.1.startCap", {"start": v(-8.2, 9.42) * mm, "mid": v(-8.95, 10.17) * mm, "end": v(-8.2, 10.92) * mm});
            skArc(sketch, "E89.1.endCap", {"start": v(8.2, 10.92) * mm, "mid": v(8.95, 10.17) * mm, "end": v(8.2, 9.42) * mm});
            skLineSegment(sketch, "E89.1.left", {"start": v(-8.2, 10.92) * mm, "end": v(8.2, 10.92) * mm});
            skLineSegment(sketch, "E89.1.right", {"start": v(-8.2, 9.42) * mm, "end": v(8.2, 9.42) * mm});
            skArc(sketch, "E89.2.startCap", {"start": v(-11, 16.75) * mm, "mid": v(-11.75, 17.5) * mm, "end": v(-11, 18.25) * mm});
            skArc(sketch, "E89.2.endCap", {"start": v(11, 18.25) * mm, "mid": v(11.75, 17.5) * mm, "end": v(11, 16.75) * mm});
            skLineSegment(sketch, "E89.2.left", {"start": v(-11, 18.25) * mm, "end": v(11, 18.25) * mm});
            skLineSegment(sketch, "E89.2.right", {"start": v(-11, 16.75) * mm, "end": v(11, 16.75) * mm});
            skArc(sketch, "E89.3.startCap", {"start": v(10.37, 21.92) * mm, "mid": v(11.12, 21.17) * mm, "end": v(10.37, 20.42) * mm});
            skArc(sketch, "E89.3.endCap", {"start": v(-10.37, 20.42) * mm, "mid": v(-11.12, 21.17) * mm, "end": v(-10.37, 21.92) * mm});
            skLineSegment(sketch, "E89.3.left", {"start": v(10.37, 20.42) * mm, "end": v(-10.37, 20.42) * mm});
            skLineSegment(sketch, "E89.3.right", {"start": v(10.37, 21.92) * mm, "end": v(-10.37, 21.92) * mm});
            skArc(sketch, "E89.4.startCap", {"start": v(10.37, 14.58) * mm, "mid": v(11.12, 13.83) * mm, "end": v(10.37, 13.08) * mm});
            skArc(sketch, "E89.4.endCap", {"start": v(-10.37, 13.08) * mm, "mid": v(-11.12, 13.83) * mm, "end": v(-10.37, 14.58) * mm});
            skLineSegment(sketch, "E89.4.left", {"start": v(10.37, 13.08) * mm, "end": v(-10.37, 13.08) * mm});
            skLineSegment(sketch, "E89.4.right", {"start": v(10.37, 14.58) * mm, "end": v(-10.37, 14.58) * mm});
            skArc(sketch, "E90.MirrorCS", {"start": v(10.37, -21.92) * mm, "mid": v(11.12, -21.17) * mm, "end": v(10.37, -20.42) * mm});
            skArc(sketch, "E91.MirrorCS", {"start": v(-10.37, -20.42) * mm, "mid": v(-11.12, -21.17) * mm, "end": v(-10.37, -21.92) * mm});
            skArc(sketch, "E92.MirrorCS", {"start": v(-10.37, -13.08) * mm, "mid": v(-11.12, -13.83) * mm, "end": v(-10.37, -14.58) * mm});
            skLineSegment(sketch, "E93.MirrorCS", {"start": v(-8.2, -24.83) * mm, "end": v(8.2, -24.83) * mm, "construction": true});
            skLineSegment(sketch, "E94.MirrorCS", {"start": v(10.37, -21.17) * mm, "end": v(-10.37, -21.17) * mm, "construction": true});
            skArc(sketch, "E95.MirrorCS", {"start": v(8.2, -10.92) * mm, "mid": v(8.95, -10.17) * mm, "end": v(8.2, -9.42) * mm});
            skArc(sketch, "E96.MirrorCS", {"start": v(11, -18.25) * mm, "mid": v(11.75, -17.5) * mm, "end": v(11, -16.75) * mm});
            skLineSegment(sketch, "E97.MirrorCS", {"start": v(10.37, -13.08) * mm, "end": v(-10.37, -13.08) * mm});
            skLineSegment(sketch, "E98.MirrorCS", {"start": v(10.37, -13.83) * mm, "end": v(-10.37, -13.83) * mm, "construction": true});
            skLineSegment(sketch, "E99.MirrorCS", {"start": v(-11, -18.25) * mm, "end": v(11, -18.25) * mm});
            skLineSegment(sketch, "E100.MirrorCS", {"start": v(-8.2, -10.17) * mm, "end": v(8.2, -10.17) * mm, "construction": true});
            skLineSegment(sketch, "E101.MirrorCS", {"start": v(-11, -17.5) * mm, "end": v(11, -17.5) * mm, "construction": true});
            skLineSegment(sketch, "E102.MirrorCS", {"start": v(-8.2, -10.92) * mm, "end": v(8.2, -10.92) * mm});
            skArc(sketch, "E103.MirrorCS", {"start": v(10.37, -14.58) * mm, "mid": v(11.12, -13.83) * mm, "end": v(10.37, -13.08) * mm});
            skLineSegment(sketch, "E104.MirrorCS", {"start": v(-8.2, -25.58) * mm, "end": v(8.2, -25.58) * mm});
            skLineSegment(sketch, "E105.MirrorCS", {"start": v(10.37, -20.42) * mm, "end": v(-10.37, -20.42) * mm});
            skArc(sketch, "E106.MirrorCS", {"start": v(-11, -16.75) * mm, "mid": v(-11.75, -17.5) * mm, "end": v(-11, -18.25) * mm});
            skLineSegment(sketch, "E107.MirrorCS", {"start": v(-8.2, -9.42) * mm, "end": v(8.2, -9.42) * mm});
            skLineSegment(sketch, "E108.MirrorCS", {"start": v(10.37, -21.92) * mm, "end": v(-10.37, -21.92) * mm});
            skLineSegment(sketch, "E109.MirrorCS", {"start": v(10.37, -14.58) * mm, "end": v(-10.37, -14.58) * mm});
            skLineSegment(sketch, "E110.MirrorCS", {"start": v(-11, -16.75) * mm, "end": v(11, -16.75) * mm});
            skArc(sketch, "E111.MirrorCS", {"start": v(-8.2, -9.42) * mm, "mid": v(-8.95, -10.17) * mm, "end": v(-8.2, -10.92) * mm});
            skArc(sketch, "E112.MirrorCS", {"start": v(-8.2, -24.08) * mm, "mid": v(-8.95, -24.83) * mm, "end": v(-8.2, -25.58) * mm});
            skLineSegment(sketch, "E113.MirrorCS", {"start": v(-8.2, -24.08) * mm, "end": v(8.2, -24.08) * mm});
            skArc(sketch, "E114.MirrorCS", {"start": v(8.2, -25.58) * mm, "mid": v(8.95, -24.83) * mm, "end": v(8.2, -24.08) * mm});
            skSolve(sketch);
        }
        {
            var Q0;
            Q0 = qSketchRegion(id + "F26", true);
            extrude(context, id + "F27", {"entities" : qUnion([Q0]), "operationType" : NewBodyOperationType.REMOVE, "endBound" : BoundingType.THROUGH_ALL, "oppositeDirection" : true, "depth" : 25 * mm});
        }
        {
            var Q0;
            Q0=makeQuery(id+"F3.opExtrude","CAP_FACE",FACE,{"disambiguationData":[OSD([sQuery(id+"F1.wireOp",EDGE,"E1"),sQuery(id+"F1.wireOp",EDGE,"E2"),sQuery(id+"F1.wireOp",EDGE,"E3"),sQuery(id+"F1.wireOp",EDGE,"E4"),sQuery(id+"F1.wireOp",EDGE,"E5"),sQuery(id+"F1.wireOp",EDGE,"E10.MirrorCS"),sQuery(id+"F1.wireOp",EDGE,"E11.MirrorCS"),sQuery(id+"F1.wireOp",EDGE,"E12.MirrorCS"),sQuery(id+"F1.wireOp",EDGE,"E13.MirrorCS"),sQuery(id+"F1.wireOp",EDGE,"E14.MirrorCS"),sQuery(id+"F1.wireOp",EDGE,"E15.MirrorCS"),sQuery(id+"F1.wireOp",EDGE,"E16.MirrorCS"),sQuery(id+"F1.wireOp",EDGE,"E17.MirrorCS"),sQuery(id+"F1.wireOp",EDGE,"E18.MirrorCS"),sQuery(id+"F1.wireOp",EDGE,"E19.MirrorCS"),sQuery(id+"F1.wireOp",EDGE,"E20.MirrorCS"),sQuery(id+"F1.wireOp",EDGE,"E21.MirrorCS"),sQuery(id+"F1.wireOp",EDGE,"E22.MirrorCS"),sQuery(id+"F1.wireOp",EDGE,"E23.MirrorCS"),sQuery(id+"F1.wireOp",EDGE,"E24.MirrorCS")])],"isStart":false});
            var sketch = newSketch(context, id + "F28", { "sketchPlane" : qUnion([Q0])});
            skText(sketch, "E115", { "text": "STRYFE", "fontName": "AllertaStencil-Regular.ttf"});
            skLineSegment(sketch, "E116", {"start": v(10.64, 0) * mm, "end": v(11.14, 0) * mm});
            skLineSegment(sketch, "E117", {"start": v(-10.64, 0) * mm, "end": v(-11.14, 0) * mm});
            const initialGuessF28  = {"E115": [-0.01016, -0.002, 1, 0, 0.00401]};
            skSetInitialGuess(sketch, initialGuessF28);
            skSolve(sketch);
        }
        {
            var Q0;
            Q0 = qSketchRegion(id + "F28", true);
            extrude(context, id + "F29", {"entities" : qUnion([Q0]), "operationType" : NewBodyOperationType.REMOVE, "oppositeDirection" : true, "depth" : .5 * mm});
        }
    });
